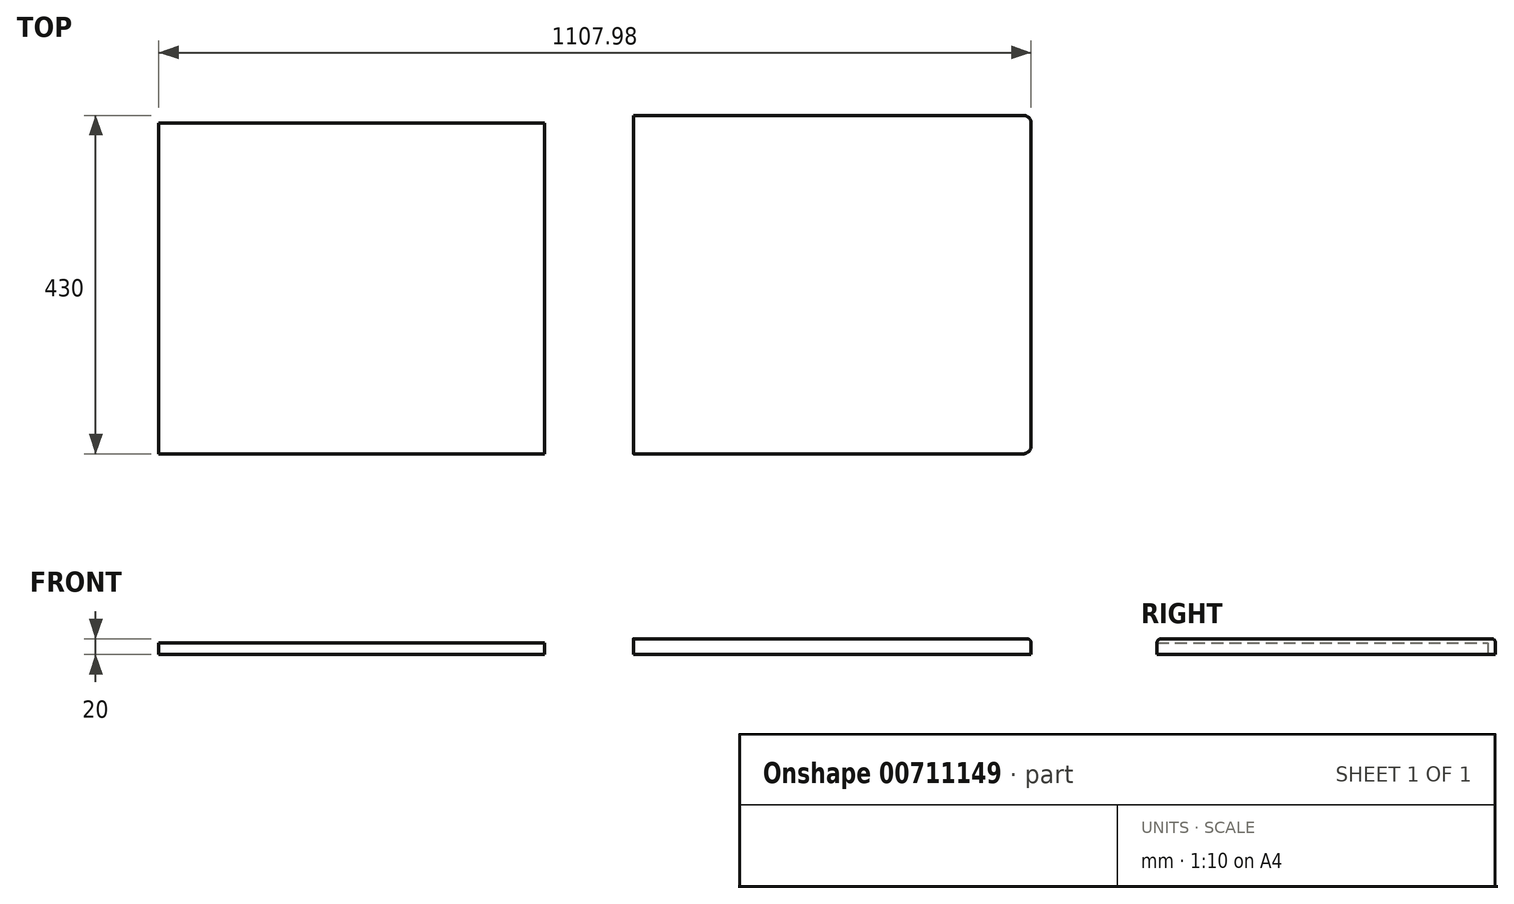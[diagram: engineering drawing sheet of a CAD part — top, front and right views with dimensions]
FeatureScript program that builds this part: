
annotation { "Feature Type Name" : "Feature", "Feature Type Description" : "" }
export const myFeature = defineFeature(function(context is Context, id is Id, definition is map)
    precondition{}
    {
        {
            var Q0;
            Q0=qCreatedBy(makeId("Top.planeOp"),FACE);
            var sketch = newSketch(context, id + "F0", { "sketchPlane" : qUnion([Q0])});
            skLineSegment(sketch, "E0.bottom", {"start": v(0, 430) * mm, "end": v(505, 430) * mm});
            skLineSegment(sketch, "E0.top", {"start": v(0, 0) * mm, "end": v(505, 0) * mm});
            skLineSegment(sketch, "E0.left", {"start": v(505, 430) * mm, "end": v(505, 0) * mm});
            skLineSegment(sketch, "E0.right", {"start": v(0, 430) * mm, "end": v(0, 0) * mm});
            skSolve(sketch);
        }
        {
            var Q0;
            Q0=makeQuery(id+"F0.imprint","IMPRINT",FACE,{"disambiguationData":[TD([[makeQuery(id+"F0.imprint","IMPRINT",EDGE,{"derivedFrom":sQuery(id+"F0.wireOp",EDGE,"E0.bottom")}),-1.0]])]});
            extrude(context, id + "F1", {"entities" : qUnion([Q0]), "depth" : 20 * mm, "offsetDistance" : 25 * mm});
        }
        {
            var Q0;
            Q0=qCreatedBy(makeId("Top.planeOp"),FACE);
            var sketch = newSketch(context, id + "F2", { "sketchPlane" : qUnion([Q0])});
            skLineSegment(sketch, "E1.bottom", {"start": v(-112.98, 0) * mm, "end": v(-602.98, 0) * mm});
            skLineSegment(sketch, "E1.top", {"start": v(-112.98, 420) * mm, "end": v(-602.98, 420) * mm});
            skLineSegment(sketch, "E1.left", {"start": v(-112.98, 0) * mm, "end": v(-112.98, 420) * mm});
            skLineSegment(sketch, "E1.right", {"start": v(-602.98, 0) * mm, "end": v(-602.98, 420) * mm});
            skSolve(sketch);
        }
        {
            var Q0;
            Q0=makeQuery(id+"F2.imprint","IMPRINT",FACE,{"disambiguationData":[TD([[makeQuery(id+"F2.imprint","IMPRINT",EDGE,{"derivedFrom":sQuery(id+"F2.wireOp",EDGE,"E1.bottom")}),-1.0]])]});
            extrude(context, id + "F3", {"entities" : qUnion([Q0]), "depth" : 15 * mm, "offsetDistance" : 25 * mm});
        }
        {
            var Q0;
            Q0=makeQuery(id+"F1.opExtrude","SWEPT_EDGE",EDGE,{"disambiguationData":[OSD([sQuery(id+"F0.wireOp",EDGE,"E0.bottom"),sQuery(id+"F0.wireOp",EDGE,"E0.left")])]});
            fillet(context, id + "F4", {"entities" : qUnion([Q0]), "radius" : 10 * mm, "tangentPropagation" : true, "allowEdgeOverflow" : false});
        }
        {
            var Q0;
            Q0=makeQuery(id+"F1.opExtrude","SWEPT_EDGE",EDGE,{"disambiguationData":[OSD([sQuery(id+"F0.wireOp",EDGE,"E0.top"),sQuery(id+"F0.wireOp",EDGE,"E0.left")])]});
            fillet(context, id + "F5", {"entities" : qUnion([Q0]), "radius" : 10 * mm, "tangentPropagation" : true, "allowEdgeOverflow" : false});
        }
        {
            var Q0;
            Q0=makeQuery(id+"F1.opExtrude","CAP_EDGE",EDGE,{"disambiguationData":[OSD([sQuery(id+"F0.wireOp",EDGE,"E0.top")])],"isStart":false});
            fillet(context, id + "F6", {"entities" : qUnion([Q0]), "radius" : 5 * mm, "tangentPropagation" : true, "allowEdgeOverflow" : false});
        }
    });
